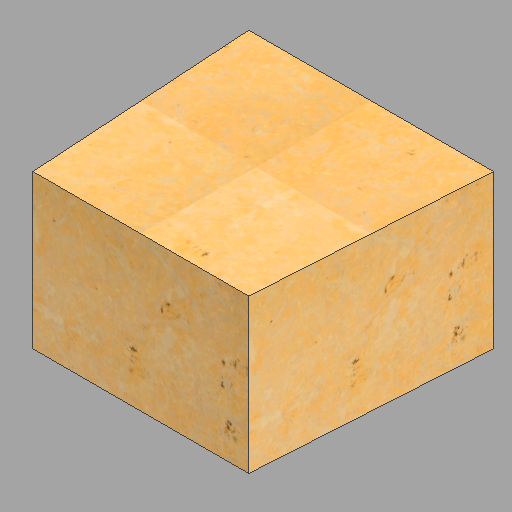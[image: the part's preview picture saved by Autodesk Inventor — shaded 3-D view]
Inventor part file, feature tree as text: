
AUTODESK INVENTOR PART (.ipt)
format: ipt  version: 2023 (Build 270158030, 158C)  size: 398,336 bytes
history: native  units: in
note: dims shown in document units (in); Inventor stores cm internally (conversion verified against a paired STEP export)
features: extrude x1, sketch x1
ambient origin geometry x8: Origin, YZ Plane, XZ Plane, XY Plane, X Axis, Y Axis, Z Axis, Center Point
bodies: Body1 (feature_tree)
feature tree (2):
  extrude  "Extrusion1"  Depth=36.0in
  sketch  "Sketch1"  dims[d0=38.25in d2=36.0in d3=0.0493in d4=2.2555in d5=2.2555in d6=24.0in d7=0.0in]
